# Revit family: ELAM STREET FRAME-HORIZONTAL MOTORISED
name_source: partatom
category: Generic Models
revit_build: Autodesk Revit 2018 (Build: 20170223_1515(x64)
units: mm (PartAtom-declared; Revit-internal decimal feet)

## family parameters
Always vertical = Yes
Can host rebar = No
Cut with Voids When Loaded = No
Part Type = Normal
Room Calculation Point = No
Round Connector Dimension = Use Diameter
Shared = No
Work Plane-Based = No

## types (1)
- ELAM STREET FRAME-HORIZONTAL MOTORISED
    200 MAXI LOUVRE BLADE = <By Category>
    ANGLE = -45.00°
    ANGLE RESTRICTION = -45.00°
    ARRAY = 10
    END CAP = <By Category>
    FRAMING = <By Category>
    HEIGHT = 2028 mm
    LEG = <By Category>
    OFFSET = 68 mm
    OVERHEAD MOTOR = LIGHT BLUE GRAY
    OVERHEAD MOTOR COVER = 900 mm  [stored 2.95276 ft]
    REMAINDER = 12 mm  [stored 0.0393701 ft]
    SPACING = 188 mm  [stored 0.616798 ft]
    WIDTH = 1500 mm  [stored 4.92126 ft]

note: [stored X ft] marks values corroborated as IEEE doubles in the binary element streams (Revit-internal decimal feet)

## geometry (parser evidence)
native form markers: Sweep x15
no freeform markers — native parametric forms only
